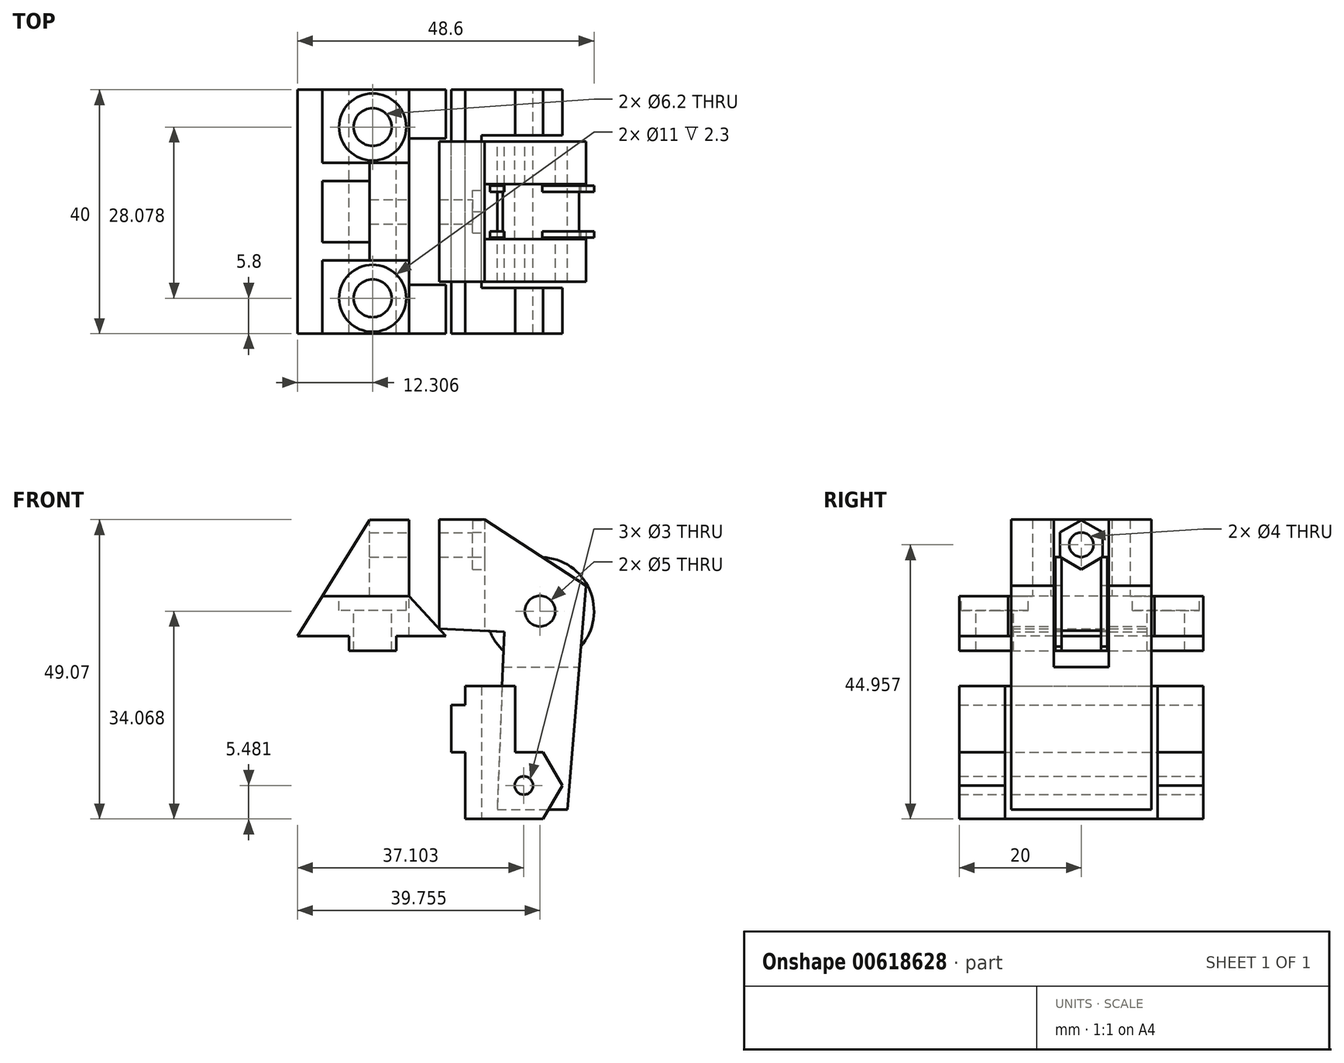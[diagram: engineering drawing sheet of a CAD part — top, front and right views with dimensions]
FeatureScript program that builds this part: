
annotation { "Feature Type Name" : "Feature", "Feature Type Description" : "" }
export const myFeature = defineFeature(function(context is Context, id is Id, definition is map)
    precondition{}
    {
        {
            var Q0;
            Q0=qCreatedBy(makeId("Front.planeOp"),FACE);
            var sketch = newSketch(context, id + "F0", { "sketchPlane" : qUnion([Q0])});
            skLineSegment(sketch, "E0.bottom", {"start": v(-16.03, 19.64) * mm, "end": v(-7.73, 19.64) * mm, "construction": true});
            skLineSegment(sketch, "E0.right", {"start": v(11.97, 17.64) * mm, "end": v(11.97, 9.34) * mm, "construction": true});
            skLineSegment(sketch, "E1.bottom", {"start": v(-11.53, 17.44) * mm, "end": v(-7.13, 17.44) * mm, "construction": true});
            skCircle(sketch, "E2", {"center": v(8.72, 16.39) * mm, "radius": 1.75 * mm, "construction": true});
            skLineSegment(sketch, "E3.trimOffspring", {"start": v(9.77, 13.14) * mm, "end": v(9.77, 8.74) * mm, "construction": true});
            skLineSegment(sketch, "E4", {"start": v(-7.13, 17.44) * mm, "end": v(-7.13, 19.14) * mm, "construction": true});
            skLineSegment(sketch, "E5", {"start": v(1.07, 17.44) * mm, "end": v(1.07, 19.14) * mm, "construction": true});
            skLineSegment(sketch, "E6.trimOffspring", {"start": v(1.67, 19.64) * mm, "end": v(9.97, 19.64) * mm, "construction": true});
            skLineSegment(sketch, "E7.trimOffspring", {"start": v(1.07, 17.44) * mm, "end": v(5.47, 17.44) * mm, "construction": true});
            skLineSegment(sketch, "E8", {"start": v(9.77, 0.54) * mm, "end": v(11.47, 0.54) * mm, "construction": true});
            skLineSegment(sketch, "E9", {"start": v(9.77, 8.74) * mm, "end": v(11.47, 8.74) * mm, "construction": true});
            skLineSegment(sketch, "E10.trimOffspring", {"start": v(11.97, -0.06) * mm, "end": v(11.97, -8.36) * mm, "construction": true});
            skLineSegment(sketch, "E11.trimOffspring", {"start": v(9.77, 0.54) * mm, "end": v(9.77, -3.86) * mm, "construction": true});
            skLineSegment(sketch, "E12.bottom", {"start": v(-7.61, 10.64) * mm, "end": v(1.56, 10.64) * mm, "construction": true});
            skLineSegment(sketch, "E12.right", {"start": v(2.97, 9.22) * mm, "end": v(2.97, 0.05) * mm, "construction": true});
            skLineSegment(sketch, "E13", {"start": v(5.47, 14.55) * mm, "end": v(5.47, 17.44) * mm, "construction": true});
            skLineSegment(sketch, "E14", {"start": v(6.89, 13.14) * mm, "end": v(9.77, 13.14) * mm, "construction": true});
            skLineSegment(sketch, "E15", {"start": v(6.89, -3.86) * mm, "end": v(9.77, -3.86) * mm, "construction": true});
            skLineSegment(sketch, "E16", {"start": v(2.97, 0.05) * mm, "end": v(6.89, -3.86) * mm, "construction": true});
            skLineSegment(sketch, "E17", {"start": v(1.56, 10.64) * mm, "end": v(5.47, 14.55) * mm, "construction": true});
            skLineSegment(sketch, "E18", {"start": v(2.97, 9.22) * mm, "end": v(6.89, 13.14) * mm, "construction": true});
            skArc(sketch, "E19.filletArc", {"start": v(-16.03, 19.64) * mm, "mid": v(-17.44, 19.05) * mm, "end": v(-18.03, 17.64) * mm, "construction": true});
            skArc(sketch, "E20.filletArc", {"start": v(11.97, 17.64) * mm, "mid": v(11.39, 19.05) * mm, "end": v(9.97, 19.64) * mm, "construction": true});
            skArc(sketch, "E21.filletArc", {"start": v(9.97, -10.36) * mm, "mid": v(11.39, -9.78) * mm, "end": v(11.97, -8.36) * mm, "construction": true});
            skLineSegment(sketch, "E22", {"start": v(11.47, 8.74) * mm, "end": v(11.47, 9.34) * mm, "construction": true});
            skLineSegment(sketch, "E23", {"start": v(11.47, 9.34) * mm, "end": v(11.97, 9.34) * mm, "construction": true});
            skLineSegment(sketch, "E24.top", {"start": v(11.97, -0.06) * mm, "end": v(11.47, -0.06) * mm, "construction": true});
            skLineSegment(sketch, "E24.right", {"start": v(11.47, 0.54) * mm, "end": v(11.47, -0.06) * mm, "construction": true});
            skLineSegment(sketch, "E25.top", {"start": v(-7.13, 19.14) * mm, "end": v(-7.73, 19.14) * mm, "construction": true});
            skLineSegment(sketch, "E25.right", {"start": v(-7.73, 19.64) * mm, "end": v(-7.73, 19.14) * mm, "construction": true});
            skLineSegment(sketch, "E26.top", {"start": v(1.07, 19.14) * mm, "end": v(1.67, 19.14) * mm, "construction": true});
            skLineSegment(sketch, "E26.right", {"start": v(1.67, 19.64) * mm, "end": v(1.67, 19.14) * mm, "construction": true});
            skLineSegment(sketch, "E27", {"start": v(9.8, 8.43) * mm, "end": v(12.04, 8.43) * mm});
            skLineSegment(sketch, "E28", {"start": v(12.04, 8.43) * mm, "end": v(12.04, 11.56) * mm});
            skLineSegment(sketch, "E29", {"start": v(2.84, 19.73) * mm, "end": v(0.74, 19.73) * mm});
            skLineSegment(sketch, "E30", {"start": v(0.74, 19.73) * mm, "end": v(0.74, 17.34) * mm});
            skLineSegment(sketch, "E31", {"start": v(9.8, 8.43) * mm, "end": v(9.8, 0.73) * mm});
            skLineSegment(sketch, "E32", {"start": v(12.04, 0.73) * mm, "end": v(12.04, -10.23) * mm});
            skLineSegment(sketch, "E33.trimOffspring", {"start": v(12.04, 0.73) * mm, "end": v(9.8, 0.73) * mm});
            skLineSegment(sketch, "E34", {"start": v(-6.96, 17.34) * mm, "end": v(-6.96, 19.73) * mm});
            skLineSegment(sketch, "E35", {"start": v(-6.96, 17.34) * mm, "end": v(0.74, 17.34) * mm});
            skPoint(sketch, "E36", {"position": v(-2.33, 17.8) * mm});
            skLineSegment(sketch, "E37", {"start": v(-6.96, 19.73) * mm, "end": v(-15.42, 19.73) * mm});
            skPoint(sketch, "E38", {"position": v(21.68, 0.73) * mm});
            skLineSegment(sketch, "E39", {"start": v(21.68, 0.73) * mm, "end": v(21.68, -10.23) * mm, "construction": true});
            skPoint(sketch, "E40", {"position": v(21.68, -4.75) * mm});
            skLineSegment(sketch, "E41.0", {"start": v(20.23, 0.73) * mm, "end": v(24.85, 0.73) * mm});
            skLineSegment(sketch, "E41.1", {"start": v(24.85, 0.73) * mm, "end": v(28.02, -4.75) * mm});
            skLineSegment(sketch, "E41.2", {"start": v(28.02, -4.75) * mm, "end": v(24.85, -10.23) * mm});
            skLineSegment(sketch, "E41.5", {"start": v(11.9, -4.75) * mm, "end": v(12.04, -4.51) * mm});
            skLineSegment(sketch, "E42.trimOffspring", {"start": v(12.04, -4.98) * mm, "end": v(11.9, -4.75) * mm});
            skCircle(sketch, "E43", {"center": v(21.68, -4.75) * mm, "radius": 1.5 * mm});
            skLineSegment(sketch, "E44", {"start": v(20.23, 0.73) * mm, "end": v(20.23, 11.56) * mm});
            skLineSegment(sketch, "E45", {"start": v(20.23, 11.56) * mm, "end": v(12.04, 11.56) * mm});
            skLineSegment(sketch, "E46", {"start": v(14.76, 11.56) * mm, "end": v(14.76, -10.23) * mm});
            skPoint(sketch, "E47", {"position": v(24.33, 23.84) * mm});
            skLineSegment(sketch, "E48", {"start": v(16.86, 23.84) * mm, "end": v(39.57, 23.84) * mm, "construction": true});
            skCircle(sketch, "E49", {"center": v(24.33, 23.84) * mm, "radius": 8.85 * mm});
            skCircle(sketch, "E50", {"center": v(24.33, 23.84) * mm, "radius": 2.5 * mm});
            skCircle(sketch, "E51", {"center": v(24.33, 23.84) * mm, "radius": 6 * mm});
            skLineSegment(sketch, "E52", {"start": v(24.85, -10.23) * mm, "end": v(12.04, -10.23) * mm});
            skLineSegment(sketch, "E53", {"start": v(7.84, 38.84) * mm, "end": v(7.84, 20.96) * mm});
            skLineSegment(sketch, "E54", {"start": v(7.84, 20.96) * mm, "end": v(18.48, 20.46) * mm});
            skLineSegment(sketch, "E55", {"start": v(18.48, 20.46) * mm, "end": v(17.3, -8.67) * mm});
            skLineSegment(sketch, "E56", {"start": v(17.3, -8.67) * mm, "end": v(28.8, -8.67) * mm});
            skLineSegment(sketch, "E57", {"start": v(28.8, -8.67) * mm, "end": v(31.86, 28) * mm});
            skLineSegment(sketch, "E58", {"start": v(31.86, 28) * mm, "end": v(15.25, 38.84) * mm});
            skLineSegment(sketch, "E59", {"start": v(15.25, 38.84) * mm, "end": v(15.25, 20.61) * mm});
            skLineSegment(sketch, "E60", {"start": v(18.25, 14.65) * mm, "end": v(30.74, 14.65) * mm});
            skLineSegment(sketch, "E61", {"start": v(15.25, 38.84) * mm, "end": v(7.84, 38.84) * mm});
            skLineSegment(sketch, "E62", {"start": v(2.84, 19.73) * mm, "end": v(2.84, 38.82) * mm});
            skLineSegment(sketch, "E63", {"start": v(2.84, 38.82) * mm, "end": v(-3.62, 38.82) * mm});
            skLineSegment(sketch, "E64", {"start": v(-3.62, 38.82) * mm, "end": v(-15.42, 19.73) * mm});
            skLineSegment(sketch, "E65", {"start": v(-11.38, 26.27) * mm, "end": v(-3.62, 26.27) * mm});
            skLineSegment(sketch, "E66", {"start": v(-3.62, 26.27) * mm, "end": v(-3.62, 38.82) * mm});
            skLineSegment(sketch, "E67", {"start": v(-3.62, 26.27) * mm, "end": v(2.84, 26.27) * mm});
            skLineSegment(sketch, "E68", {"start": v(2.84, 26.27) * mm, "end": v(8.9, 19.73) * mm});
            skLineSegment(sketch, "E69", {"start": v(8.9, 19.73) * mm, "end": v(2.84, 19.73) * mm});
            skSolve(sketch);
        }
        {
            var Q0;
            {var subQ4=sQuery(id+"F0.wireOp",EDGE,"E27");Q0=makeQuery(id+"F0.imprint","IMPRINT",FACE,{"disambiguationData":[TD([[makeQuery(id+"F0.imprint","IMPRINT",EDGE,{"derivedFrom":subQ4}),-1.0]])]});}
            var Q1;
            {var subQ0=sQuery(id+"F0.wireOp",EDGE,"E46");Q1=makeQuery(id+"F0.imprint","IMPRINT",FACE,{"disambiguationData":[TD([[makeQuery(id+"F0.imprint","IMPRINT",EDGE,{"derivedFrom":subQ0}),1.0]])]});}
            var Q2;
            Q2=makeQuery(id+"F0.imprint","IMPRINT",FACE,{"disambiguationData":[TD([[makeQuery(id+"F0.imprint","IMPRINT",EDGE,{"derivedFrom":sQuery(id+"F0.wireOp",EDGE,"E41.0")}),-1.0]])]});
            extrude(context, id + "F1", {"entities" : qUnion([Q0, Q1, Q2]), "endBound" : BoundingType.SYMMETRIC, "depth" : 40 * mm, "offsetDistance" : 25 * mm});
        }
        {
            var Q0;
            Q0=makeQuery(id+"F0.imprint","IMPRINT",FACE,{"disambiguationData":[TD([[makeQuery(id+"F0.imprint","IMPRINT",EDGE,{"derivedFrom":sQuery(id+"F0.wireOp",EDGE,"E41.0")}),-1.0]])]});
            var Q1;
            {var subQ0=sQuery(id+"F0.wireOp",EDGE,"E46");Q1=makeQuery(id+"F0.imprint","IMPRINT",FACE,{"disambiguationData":[TD([[makeQuery(id+"F0.imprint","IMPRINT",EDGE,{"derivedFrom":subQ0}),1.0]])]});}
            extrude(context, id + "F2", {"entities" : qUnion([Q0, Q1]), "operationType" : NewBodyOperationType.REMOVE, "endBound" : BoundingType.SYMMETRIC, "depth" : 25 * mm, "offsetDistance" : 25 * mm});
        }
        {
            var Q0;
            Q0=makeQuery(id+"F0.imprint","IMPRINT",FACE,{"disambiguationData":[TD([[makeQuery(id+"F0.imprint","IMPRINT",EDGE,{"derivedFrom":sQuery(id+"F0.wireOp",EDGE,"E49")}),1.0]])]});
            var Q1;
            Q1=makeQuery(id+"F0.imprint","IMPRINT",FACE,{"disambiguationData":[TD([[makeQuery(id+"F0.imprint","IMPRINT",EDGE,{"derivedFrom":sQuery(id+"F0.wireOp",EDGE,"E50")}),-1.0]])]});
            var Q2;
            {var subQ0=sQuery(id+"F0.wireOp",EDGE,"E58");var subQ1=sQuery(id+"F0.wireOp",EDGE,"E51");var subQ2=makeQuery(id+"F0.imprint","INTERSECT",VERTEX,{"disambiguationData":[OD(0.0)],"derivedFrom":[subQ1,subQ0]});Q2=makeQuery(id+"F0.imprint","IMPRINT",FACE,{"disambiguationData":[TD([[makeQuery(id+"F0.imprint","IMPRINT",EDGE,{"disambiguationData":[TD([[subQ2,-1.0]])],"derivedFrom":subQ1}),1.0]])]});}
            var Q3;
            {var subQ0=sQuery(id+"F0.wireOp",EDGE,"E58");var subQ5=sQuery(id+"F0.wireOp",EDGE,"E49");var subQ8=makeQuery(id+"F0.imprint","INTERSECT",VERTEX,{"derivedFrom":[subQ5,subQ0]});Q3=makeQuery(id+"F0.imprint","IMPRINT",FACE,{"disambiguationData":[TD([[makeQuery(id+"F0.imprint","IMPRINT",EDGE,{"disambiguationData":[TD([[subQ8,1.0]])],"derivedFrom":subQ5}),1.0]])]});}
            var Q4;
            {var subQ0=sQuery(id+"F0.wireOp",EDGE,"E54");var subQ1=sQuery(id+"F0.wireOp",EDGE,"E49");var subQ2=makeQuery(id+"F0.imprint","INTERSECT",VERTEX,{"derivedFrom":[subQ1,subQ0]});Q4=makeQuery(id+"F0.imprint","IMPRINT",FACE,{"disambiguationData":[TD([[makeQuery(id+"F0.imprint","IMPRINT",EDGE,{"disambiguationData":[TD([[subQ2,-1.0]])],"derivedFrom":subQ1}),1.0]])]});}
            extrude(context, id + "F3", {"entities" : qUnion([Q0, Q1, Q2, Q3, Q4]), "endBound" : BoundingType.SYMMETRIC, "depth" : 8.5 * mm, "offsetDistance" : 25 * mm});
        }
        {
            var Q0;
            {var subQ0=sQuery(id+"F0.wireOp",EDGE,"E58");var subQ5=sQuery(id+"F0.wireOp",EDGE,"E49");var subQ8=makeQuery(id+"F0.imprint","INTERSECT",VERTEX,{"derivedFrom":[subQ5,subQ0]});Q0=makeQuery(id+"F0.imprint","IMPRINT",FACE,{"disambiguationData":[TD([[makeQuery(id+"F0.imprint","IMPRINT",EDGE,{"disambiguationData":[TD([[subQ8,1.0]])],"derivedFrom":subQ5}),1.0]])]});}
            var Q1;
            {var subQ5=sQuery(id+"F0.wireOp",EDGE,"E54");var subQ7=sQuery(id+"F0.wireOp",EDGE,"E49");var subQ8=makeQuery(id+"F0.imprint","INTERSECT",VERTEX,{"derivedFrom":[subQ7,subQ5]});Q1=makeQuery(id+"F0.imprint","IMPRINT",FACE,{"disambiguationData":[TD([[makeQuery(id+"F0.imprint","IMPRINT",EDGE,{"disambiguationData":[TD([[subQ8,1.0]])],"derivedFrom":subQ7}),1.0]])]});}
            var Q2;
            {var subQ0=sQuery(id+"F0.wireOp",EDGE,"E54");var subQ1=sQuery(id+"F0.wireOp",EDGE,"E49");var subQ2=makeQuery(id+"F0.imprint","INTERSECT",VERTEX,{"derivedFrom":[subQ1,subQ0]});Q2=makeQuery(id+"F0.imprint","IMPRINT",FACE,{"disambiguationData":[TD([[makeQuery(id+"F0.imprint","IMPRINT",EDGE,{"disambiguationData":[TD([[subQ2,-1.0]])],"derivedFrom":subQ1}),1.0]])]});}
            extrude(context, id + "F4", {"entities" : qUnion([Q0, Q1, Q2]), "operationType" : NewBodyOperationType.REMOVE, "endBound" : BoundingType.SYMMETRIC, "oppositeDirection" : true, "depth" : 6.5 * mm, "offsetDistance" : 25 * mm});
        }
        {
            var Q0;
            Q0=makeQuery(id+"F0.imprint","IMPRINT",FACE,{"disambiguationData":[TD([[makeQuery(id+"F0.imprint","IMPRINT",EDGE,{"derivedFrom":sQuery(id+"F0.wireOp",EDGE,"E41.0")}),-1.0]])]});
            var Q1;
            Q1=makeQuery(id+"F0.imprint","IMPRINT",FACE,{"disambiguationData":[TD([[makeQuery(id+"F0.imprint","IMPRINT",EDGE,{"derivedFrom":sQuery(id+"F0.wireOp",EDGE,"E41.0")}),1.0]])]});
            var Q2;
            {var subQ5=sQuery(id+"F0.wireOp",EDGE,"E60");Q2=makeQuery(id+"F0.imprint","IMPRINT",FACE,{"disambiguationData":[TD([[makeQuery(id+"F0.imprint","IMPRINT",EDGE,{"derivedFrom":subQ5}),1.0]])]});}
            var Q3;
            Q3=makeQuery(id+"F0.imprint","IMPRINT",FACE,{"disambiguationData":[TD([[makeQuery(id+"F0.imprint","IMPRINT",EDGE,{"derivedFrom":sQuery(id+"F0.wireOp",EDGE,"E50")}),-1.0]])]});
            var Q4;
            {var subQ5=sQuery(id+"F0.wireOp",EDGE,"E54");var subQ7=sQuery(id+"F0.wireOp",EDGE,"E49");var subQ8=makeQuery(id+"F0.imprint","INTERSECT",VERTEX,{"derivedFrom":[subQ7,subQ5]});Q4=makeQuery(id+"F0.imprint","IMPRINT",FACE,{"disambiguationData":[TD([[makeQuery(id+"F0.imprint","IMPRINT",EDGE,{"disambiguationData":[TD([[subQ8,1.0]])],"derivedFrom":subQ7}),1.0]])]});}
            var Q5;
            {var subQ0=sQuery(id+"F0.wireOp",EDGE,"muFqakcZ-oCHJ-JS1d-ti05-DOdv9Udi4cEH");Q5=makeQuery(id+"F0.imprint","IMPRINT",FACE,{"disambiguationData":[TD([[makeQuery(id+"F0.imprint","IMPRINT",EDGE,{"derivedFrom":subQ0}),1.0]])]});}
            var Q6;
            {var subQ2=sQuery(id+"F0.wireOp",EDGE,"E53");Q6=makeQuery(id+"F0.imprint","IMPRINT",FACE,{"disambiguationData":[TD([[makeQuery(id+"F0.imprint","IMPRINT",EDGE,{"derivedFrom":subQ2}),1.0]])]});}
            var Q7;
            {var subQ5=sQuery(id+"F0.wireOp",EDGE,"E59");Q7=makeQuery(id+"F0.imprint","IMPRINT",FACE,{"disambiguationData":[TD([[makeQuery(id+"F0.imprint","IMPRINT",EDGE,{"derivedFrom":subQ5}),1.0]])]});}
            extrude(context, id + "F5", {"entities" : qUnion([Q0, Q1, Q2, Q3, Q4, Q5, Q6, Q7]), "endBound" : BoundingType.SYMMETRIC, "depth" : 23 * mm, "offsetDistance" : 25 * mm});
        }
        {
            var Q0;
            {var subQ0=sQuery(id+"F0.wireOp",EDGE,"muFqakcZ-oCHJ-JS1d-ti05-DOdv9Udi4cEH");Q0=makeQuery(id+"F0.imprint","IMPRINT",FACE,{"disambiguationData":[TD([[makeQuery(id+"F0.imprint","IMPRINT",EDGE,{"derivedFrom":subQ0}),1.0]])]});}
            var Q1;
            {var subQ5=sQuery(id+"F0.wireOp",EDGE,"E54");var subQ7=sQuery(id+"F0.wireOp",EDGE,"E49");var subQ8=makeQuery(id+"F0.imprint","INTERSECT",VERTEX,{"derivedFrom":[subQ7,subQ5]});Q1=makeQuery(id+"F0.imprint","IMPRINT",FACE,{"disambiguationData":[TD([[makeQuery(id+"F0.imprint","IMPRINT",EDGE,{"disambiguationData":[TD([[subQ8,1.0]])],"derivedFrom":subQ7}),1.0]])]});}
            var Q2;
            Q2=makeQuery(id+"F0.imprint","IMPRINT",FACE,{"disambiguationData":[TD([[makeQuery(id+"F0.imprint","IMPRINT",EDGE,{"derivedFrom":sQuery(id+"F0.wireOp",EDGE,"E50")}),-1.0]])]});
            var Q3;
            Q3=makeQuery(id+"F0.imprint","IMPRINT",FACE,{"disambiguationData":[TD([[makeQuery(id+"F0.imprint","IMPRINT",EDGE,{"derivedFrom":sQuery(id+"F0.wireOp",EDGE,"E50")}),1.0]])]});
            var Q4;
            {var subQ5=sQuery(id+"F0.wireOp",EDGE,"E60");Q4=makeQuery(id+"F0.imprint","IMPRINT",FACE,{"disambiguationData":[TD([[makeQuery(id+"F0.imprint","IMPRINT",EDGE,{"derivedFrom":subQ5}),1.0]])]});}
            var Q5;
            {var subQ5=sQuery(id+"F0.wireOp",EDGE,"E59");Q5=makeQuery(id+"F0.imprint","IMPRINT",FACE,{"disambiguationData":[TD([[makeQuery(id+"F0.imprint","IMPRINT",EDGE,{"derivedFrom":subQ5}),1.0]])]});}
            extrude(context, id + "F6", {"entities" : qUnion([Q0, Q1, Q2, Q3, Q4, Q5]), "operationType" : NewBodyOperationType.REMOVE, "endBound" : BoundingType.SYMMETRIC, "oppositeDirection" : true, "depth" : 9 * mm, "offsetDistance" : 25 * mm});
        }
        {
            var Q0;
            {var subQ3=sQuery(id+"F0.wireOp",EDGE,"E29");Q0=makeQuery(id+"F0.imprint","IMPRINT",FACE,{"disambiguationData":[TD([[makeQuery(id+"F0.imprint","IMPRINT",EDGE,{"derivedFrom":subQ3}),-1.0]])]});}
            var Q1;
            {var subQ2=sQuery(id+"F0.wireOp",EDGE,"E68");Q1=makeQuery(id+"F0.imprint","IMPRINT",FACE,{"disambiguationData":[TD([[makeQuery(id+"F0.imprint","IMPRINT",EDGE,{"derivedFrom":subQ2}),-1.0]])]});}
            extrude(context, id + "F7", {"entities" : qUnion([Q0, Q1]), "endBound" : BoundingType.SYMMETRIC, "depth" : 40 * mm, "offsetDistance" : 25 * mm});
        }
        {
            var Q0;
            {var subQ0=sQuery(id+"F0.wireOp",EDGE,"E63");Q0=makeQuery(id+"F0.imprint","IMPRINT",FACE,{"disambiguationData":[TD([[makeQuery(id+"F0.imprint","IMPRINT",EDGE,{"derivedFrom":subQ0}),1.0]])]});}
            var Q1;
            {var subQ2=sQuery(id+"F0.wireOp",EDGE,"E65");Q1=makeQuery(id+"F0.imprint","IMPRINT",FACE,{"disambiguationData":[TD([[makeQuery(id+"F0.imprint","IMPRINT",EDGE,{"derivedFrom":subQ2}),1.0]])]});}
            extrude(context, id + "F8", {"entities" : qUnion([Q0, Q1]), "operationType" : NewBodyOperationType.ADD, "endBound" : BoundingType.SYMMETRIC, "depth" : 16 * mm, "offsetDistance" : 25 * mm});
        }
        {
            var Q0;
            {var subQ2=sQuery(id+"F0.wireOp",EDGE,"E65");Q0=makeQuery(id+"F0.imprint","IMPRINT",FACE,{"disambiguationData":[TD([[makeQuery(id+"F0.imprint","IMPRINT",EDGE,{"derivedFrom":subQ2}),1.0]])]});}
            extrude(context, id + "F9", {"entities" : qUnion([Q0]), "operationType" : NewBodyOperationType.REMOVE, "endBound" : BoundingType.SYMMETRIC, "oppositeDirection" : true, "depth" : 10 * mm, "offsetDistance" : 25 * mm});
        }
        {
            var Q0;
            Q0=makeQuery(id+"F6.boolean.opBoolean","COPY",FACE,{"derivedFrom":makeQuery(id+"F6.opExtrude","SWEPT_FACE",FACE,{"disambiguationData":[OSD([sQuery(id+"F0.wireOp",EDGE,"E59")])]})});
            var sketch = newSketch(context, id + "F10", { "sketchPlane" : qUnion([Q0])});
            skLineSegment(sketch, "E70.0", {"start": v(0, 19.73) * mm, "end": v(0, 38.77) * mm, "construction": true});
            skCircle(sketch, "E71.cCircle", {"center": v(0, 34.73) * mm, "radius": 3.5 * mm, "construction": true});
            skLineSegment(sketch, "E71.0", {"start": v(0, 38.77) * mm, "end": v(3.5, 36.75) * mm});
            skLineSegment(sketch, "E71.1", {"start": v(3.5, 36.75) * mm, "end": v(3.5, 32.7) * mm});
            skLineSegment(sketch, "E71.2", {"start": v(3.5, 32.7) * mm, "end": v(0, 30.69) * mm});
            skLineSegment(sketch, "E71.3", {"start": v(0, 30.69) * mm, "end": v(-3.5, 32.7) * mm});
            skLineSegment(sketch, "E71.4", {"start": v(-3.5, 32.7) * mm, "end": v(-3.5, 36.75) * mm});
            skLineSegment(sketch, "E71.5", {"start": v(-3.5, 36.75) * mm, "end": v(0, 38.77) * mm});
            skPoint(sketch, "E71.0.midPoint", {"position": v(1.75, 37.76) * mm});
            skCircle(sketch, "E72", {"center": v(0, 34.73) * mm, "radius": 2 * mm});
            skSolve(sketch);
        }
        {
            var Q0;
            Q0=makeQuery(id+"F10.imprint","IMPRINT",FACE,{"disambiguationData":[TD([[makeQuery(id+"F10.imprint","IMPRINT",EDGE,{"derivedFrom":sQuery(id+"F10.wireOp",EDGE,"E72")}),1.0]])]});
            extrude(context, id + "F11", {"entities" : qUnion([Q0]), "operationType" : NewBodyOperationType.REMOVE, "oppositeDirection" : true, "depth" : 25 * mm, "offsetDistance" : 25 * mm});
        }
        {
            var Q0;
            {var subQ8=sQuery(id+"F10.wireOp",EDGE,"E71.1");Q0=makeQuery(id+"F10.imprint","IMPRINT",FACE,{"disambiguationData":[TD([[makeQuery(id+"F10.imprint","IMPRINT",EDGE,{"derivedFrom":subQ8}),-1.0]])]});}
            extrude(context, id + "F12", {"entities" : qUnion([Q0]), "operationType" : NewBodyOperationType.REMOVE, "oppositeDirection" : true, "depth" : 2 * mm, "offsetDistance" : 25 * mm});
        }
        {
            var Q0;
            {var subQ0=sQuery(id+"F0.wireOp",EDGE,"E62");var subQ1=sQuery(id+"F0.wireOp",EDGE,"E64");var subQ2=sQuery(id+"F0.wireOp",EDGE,"E67");var subQ3=sQuery(id+"F0.wireOp",EDGE,"E65");Q0=makeQuery(id+"F8.boolean.opBoolean","SPLIT",FACE,{"disambiguationData":[TD([makeQuery(id+"F8.opExtrude","CAP_FACE",FACE,{"disambiguationData":[OSD([subQ0,sQuery(id+"F0.wireOp",EDGE,"E63"),subQ1,subQ3,subQ2])],"isStart":false})])],"derivedFrom":makeQuery(id+"F7.opExtrude","SWEPT_FACE",FACE,{"disambiguationData":[OSD([subQ3,subQ2])]})});}
            var sketch = newSketch(context, id + "F13", { "sketchPlane" : qUnion([Q0])});
            skCircle(sketch, "E73", {"center": v(-3.11, -14.2) * mm, "radius": 3.1 * mm});
            skCircle(sketch, "E74", {"center": v(-3.11, -14.2) * mm, "radius": 5.5 * mm});
            skPoint(sketch, "E75.0", {"position": v(4.39, -14.2) * mm});
            skLineSegment(sketch, "E76", {"start": v(4.39, -14.2) * mm, "end": v(-10.61, -14.2) * mm, "construction": true});
            skCircle(sketch, "E77", {"center": v(-3.11, 13.88) * mm, "radius": 3.1 * mm});
            skCircle(sketch, "E78", {"center": v(-3.11, 13.88) * mm, "radius": 5.5 * mm});
            skPoint(sketch, "E79.0", {"position": v(4.39, 13.88) * mm});
            skLineSegment(sketch, "E80", {"start": v(4.39, 13.88) * mm, "end": v(-10.61, 13.88) * mm, "construction": true});
            skSolve(sketch);
        }
        {
            var Q0;
            Q0=makeQuery(id+"F13.imprint","IMPRINT",FACE,{"disambiguationData":[TD([[makeQuery(id+"F13.imprint","IMPRINT",EDGE,{"derivedFrom":sQuery(id+"F13.wireOp",EDGE,"E77")}),1.0]])]});
            var Q1;
            {var subQ0=sQuery(id+"F13.wireOp",EDGE,"E73");var subQ1=sQuery(id+"F0.wireOp",EDGE,"E62");var subQ2=sQuery(id+"F0.wireOp",EDGE,"E64");var subQ3=sQuery(id+"F0.wireOp",EDGE,"E67");var subQ4=sQuery(id+"F0.wireOp",EDGE,"E65");var subQ5=makeQuery(id+"F74KQNxXO5Mzhl8_3.opChamfer","BLEND_EDGE",EDGE,{"blendedFrom":[makeQuery(id+"F8.opExtrude","CAP_EDGE",EDGE,{"disambiguationData":[OSD([subQ4,subQ3])],"isStart":false}),makeQuery(id+"F8.boolean.opBoolean","SPLIT",FACE,{"disambiguationData":[TD([makeQuery(id+"F8.opExtrude","CAP_FACE",FACE,{"disambiguationData":[OSD([subQ1,sQuery(id+"F0.wireOp",EDGE,"E63"),subQ2,subQ4,subQ3])],"isStart":false})])],"derivedFrom":makeQuery(id+"F7.opExtrude","SWEPT_FACE",FACE,{"disambiguationData":[OSD([subQ4,subQ3])]})})],"blendedInto":[makeQuery(id+"F8.boolean.opBoolean","SPLIT",FACE,{"disambiguationData":[TD([makeQuery(id+"F8.opExtrude","CAP_FACE",FACE,{"disambiguationData":[OSD([subQ1,sQuery(id+"F0.wireOp",EDGE,"E63"),subQ2,subQ4,subQ3])],"isStart":false})])],"derivedFrom":makeQuery(id+"F7.opExtrude","SWEPT_FACE",FACE,{"disambiguationData":[OSD([subQ4,subQ3])]})})]});var subQ6=makeQuery(id+"F13.imprint","INTERSECT",VERTEX,{"disambiguationData":[OD(0.0)],"derivedFrom":[subQ5,subQ0]});Q1=makeQuery(id+"F13.imprint","IMPRINT",FACE,{"disambiguationData":[TD([[makeQuery(id+"F13.imprint","IMPRINT",EDGE,{"disambiguationData":[TD([[subQ6,-1.0]])],"derivedFrom":subQ0}),1.0]])]});}
            var Q2;
            {var subQ0=sQuery(id+"F13.wireOp",EDGE,"E73");var subQ1=sQuery(id+"F0.wireOp",EDGE,"E62");var subQ2=sQuery(id+"F0.wireOp",EDGE,"E64");var subQ3=sQuery(id+"F0.wireOp",EDGE,"E67");var subQ4=sQuery(id+"F0.wireOp",EDGE,"E65");var subQ5=makeQuery(id+"F74KQNxXO5Mzhl8_3.opChamfer","BLEND_EDGE",EDGE,{"blendedFrom":[makeQuery(id+"F8.opExtrude","CAP_EDGE",EDGE,{"disambiguationData":[OSD([subQ4,subQ3])],"isStart":false}),makeQuery(id+"F8.boolean.opBoolean","SPLIT",FACE,{"disambiguationData":[TD([makeQuery(id+"F8.opExtrude","CAP_FACE",FACE,{"disambiguationData":[OSD([subQ1,sQuery(id+"F0.wireOp",EDGE,"E63"),subQ2,subQ4,subQ3])],"isStart":false})])],"derivedFrom":makeQuery(id+"F7.opExtrude","SWEPT_FACE",FACE,{"disambiguationData":[OSD([subQ4,subQ3])]})})],"blendedInto":[makeQuery(id+"F8.boolean.opBoolean","SPLIT",FACE,{"disambiguationData":[TD([makeQuery(id+"F8.opExtrude","CAP_FACE",FACE,{"disambiguationData":[OSD([subQ1,sQuery(id+"F0.wireOp",EDGE,"E63"),subQ2,subQ4,subQ3])],"isStart":false})])],"derivedFrom":makeQuery(id+"F7.opExtrude","SWEPT_FACE",FACE,{"disambiguationData":[OSD([subQ4,subQ3])]})})]});var subQ6=makeQuery(id+"F13.imprint","INTERSECT",VERTEX,{"disambiguationData":[OD(0.0)],"derivedFrom":[subQ5,subQ0]});Q2=makeQuery(id+"F13.imprint","IMPRINT",FACE,{"disambiguationData":[TD([[makeQuery(id+"F13.imprint","IMPRINT",EDGE,{"disambiguationData":[TD([[subQ6,1.0]])],"derivedFrom":subQ0}),1.0]])]});}
            var Q3;
            Q3=makeQuery(id+"F13.imprint","IMPRINT",FACE,{"disambiguationData":[TD([[makeQuery(id+"F13.imprint","IMPRINT",EDGE,{"derivedFrom":sQuery(id+"F13.wireOp",EDGE,"E73")}),1.0]])]});
            extrude(context, id + "F14", {"entities" : qUnion([Q0, Q1, Q2, Q3]), "operationType" : NewBodyOperationType.REMOVE, "endBound" : BoundingType.SYMMETRIC, "oppositeDirection" : true, "depth" : 19.2 * mm, "offsetDistance" : 25 * mm});
        }
        {
            var Q0;
            Q0=makeQuery(id+"F13.imprint","IMPRINT",FACE,{"disambiguationData":[TD([[makeQuery(id+"F13.imprint","IMPRINT",EDGE,{"derivedFrom":sQuery(id+"F13.wireOp",EDGE,"E77")}),-1.0]])]});
            var Q1;
            {var subQ0=sQuery(id+"F0.wireOp",EDGE,"E67");var subQ1=sQuery(id+"F0.wireOp",EDGE,"E65");var subQ3=sQuery(id+"F0.wireOp",EDGE,"E64");var subQ4=sQuery(id+"F0.wireOp",EDGE,"E62");var subQ5=makeQuery(id+"F8.opExtrude","CAP_FACE",FACE,{"disambiguationData":[OSD([subQ4,sQuery(id+"F0.wireOp",EDGE,"E63"),subQ3,subQ1,subQ0])],"isStart":false});var subQ9=makeQuery(id+"F8.boolean.opBoolean","SPLIT",EDGE,{"disambiguationData":[TD([subQ5])],"derivedFrom":makeQuery(id+"F7.opExtrude","SWEPT_EDGE",EDGE,{"disambiguationData":[OSD([subQ3,subQ1])]})});var subQ12=sQuery(id+"F13.wireOp",EDGE,"E74");var subQ13=makeQuery(id+"F13.imprint","INTERSECT",VERTEX,{"derivedFrom":[subQ9,subQ12]});Q1=makeQuery(id+"F13.imprint","IMPRINT",FACE,{"disambiguationData":[TD([[makeQuery(id+"F13.imprint","IMPRINT",EDGE,{"disambiguationData":[TD([[subQ13,-1.0]])],"derivedFrom":subQ12}),1.0]])]});}
            var Q2;
            {var subQ0=sQuery(id+"F0.wireOp",EDGE,"E67");var subQ1=sQuery(id+"F0.wireOp",EDGE,"E65");var subQ3=sQuery(id+"F0.wireOp",EDGE,"E64");var subQ4=sQuery(id+"F0.wireOp",EDGE,"E62");var subQ5=makeQuery(id+"F8.opExtrude","CAP_FACE",FACE,{"disambiguationData":[OSD([subQ4,sQuery(id+"F0.wireOp",EDGE,"E63"),subQ3,subQ1,subQ0])],"isStart":false});var subQ9=makeQuery(id+"F8.boolean.opBoolean","SPLIT",EDGE,{"disambiguationData":[TD([subQ5])],"derivedFrom":makeQuery(id+"F7.opExtrude","SWEPT_EDGE",EDGE,{"disambiguationData":[OSD([subQ3,subQ1])]})});var subQ14=sQuery(id+"F13.wireOp",EDGE,"E74");var subQ15=makeQuery(id+"F13.imprint","INTERSECT",VERTEX,{"derivedFrom":[subQ9,subQ14]});Q2=makeQuery(id+"F13.imprint","IMPRINT",FACE,{"disambiguationData":[TD([[makeQuery(id+"F13.imprint","IMPRINT",EDGE,{"disambiguationData":[TD([[subQ15,1.0]])],"derivedFrom":subQ14}),1.0]])]});}
            var Q3;
            Q3=makeQuery(id+"F13.imprint","IMPRINT",FACE,{"disambiguationData":[TD([[makeQuery(id+"F13.imprint","IMPRINT",EDGE,{"derivedFrom":sQuery(id+"F13.wireOp",EDGE,"E73")}),-1.0]])]});
            extrude(context, id + "F15", {"entities" : qUnion([Q0, Q1, Q2, Q3]), "operationType" : NewBodyOperationType.REMOVE, "endBound" : BoundingType.SYMMETRIC, "oppositeDirection" : true, "depth" : 4.6 * mm, "offsetDistance" : 25 * mm});
        }
        {
            var Q0;
            {var subQ2=sQuery(id+"F0.wireOp",EDGE,"E68");Q0=makeQuery(id+"F0.imprint","IMPRINT",FACE,{"disambiguationData":[TD([[makeQuery(id+"F0.imprint","IMPRINT",EDGE,{"derivedFrom":subQ2}),-1.0]])]});}
            extrude(context, id + "F16", {"entities" : qUnion([Q0]), "operationType" : NewBodyOperationType.REMOVE, "endBound" : BoundingType.SYMMETRIC, "oppositeDirection" : true, "depth" : 24 * mm, "offsetDistance" : 25 * mm});
        }
        {
            var Q0;
            Q0=makeQuery(id+"F3.opExtrude","SWEPT_BODY",BODY,{"disambiguationData":[OSD([sQuery(id+"F0.wireOp",EDGE,"E49"),sQuery(id+"F0.wireOp",EDGE,"E50")])]});
            transform(context, id + "F17", {"entities" : qUnion([Q0]), "transformType" : TransformType.TRANSLATION_3D, "dx" : 0 * mm, "dy" : 0 * mm, "dz" : 0 * mm, "makeCopy" : true});
        }
    });
